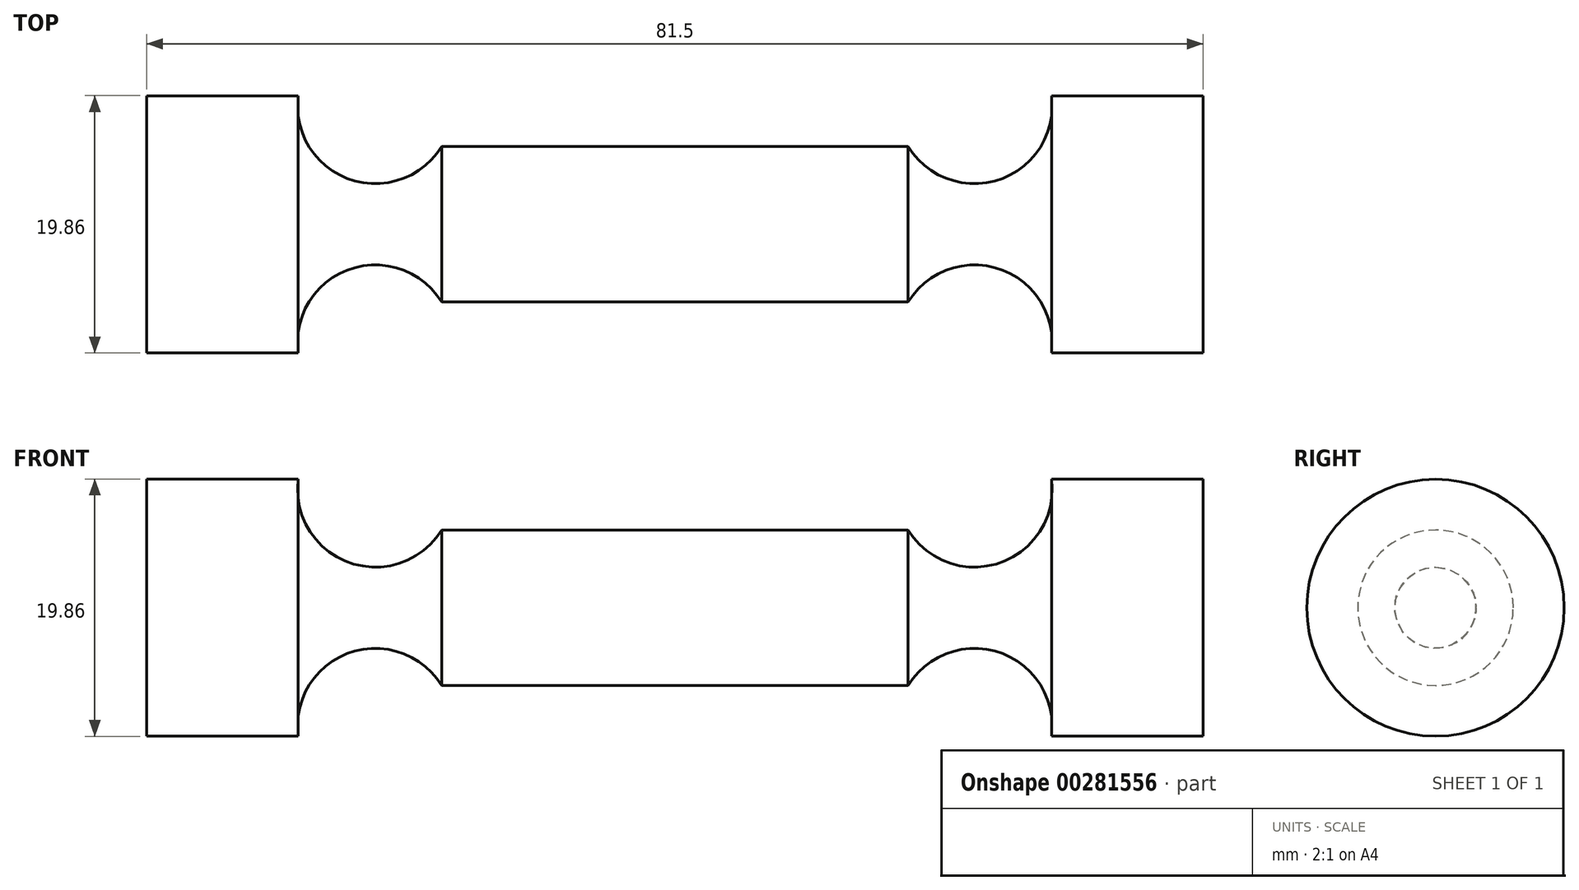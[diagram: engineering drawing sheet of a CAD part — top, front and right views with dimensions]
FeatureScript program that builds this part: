
annotation { "Feature Type Name" : "Feature", "Feature Type Description" : "" }
export const myFeature = defineFeature(function(context is Context, id is Id, definition is map)
    precondition{}
    {
        {
            var Q0;
            Q0=qCreatedBy(makeId("Front.planeOp"),FACE);
            var sketch = newSketch(context, id + "F0", { "sketchPlane" : qUnion([Q0])});
            skLineSegment(sketch, "E0", {"start": v(0, 6) * mm, "end": v(18, 6) * mm});
            skArc(sketch, "E1", {"start": v(18, 6) * mm, "mid": v(25.12, 3.48) * mm, "end": v(29.06, 9.93) * mm});
            skLineSegment(sketch, "E2", {"start": v(29.06, 9.93) * mm, "end": v(40.75, 9.93) * mm});
            skLineSegment(sketch, "E3", {"start": v(40.75, 9.93) * mm, "end": v(40.75, 0) * mm});
            skLineSegment(sketch, "E4.MirrorCS", {"start": v(-29.06, 9.93) * mm, "end": v(-40.75, 9.93) * mm});
            skArc(sketch, "E5.MirrorCS", {"start": v(-18, 6) * mm, "mid": v(-25.12, 3.48) * mm, "end": v(-29.06, 9.93) * mm});
            skLineSegment(sketch, "E6.MirrorCS", {"start": v(0, 6) * mm, "end": v(-18, 6) * mm});
            skLineSegment(sketch, "E7.MirrorCS", {"start": v(-40.75, 9.93) * mm, "end": v(-40.75, 0) * mm});
            skLineSegment(sketch, "E8", {"start": v(-40.75, 0) * mm, "end": v(40.75, 0) * mm});
            skSolve(sketch);
        }
        {
            var Q0;
            Q0=makeQuery(id+"F0.imprint","IMPRINT",FACE,{"disambiguationData":[TD([[makeQuery(id+"F0.imprint","IMPRINT",EDGE,{"derivedFrom":sQuery(id+"F0.wireOp",EDGE,"E0")}),-1.0]])]});
            var Q1;
            Q1=sQuery(id+"F0.wireOp",EDGE,"E8");
            revolve(context, id + "F1", {"entities" : qUnion([Q0]), "axis" : qUnion([Q1]), "revolveType" : RevolveType.FULL});
        }
    });
